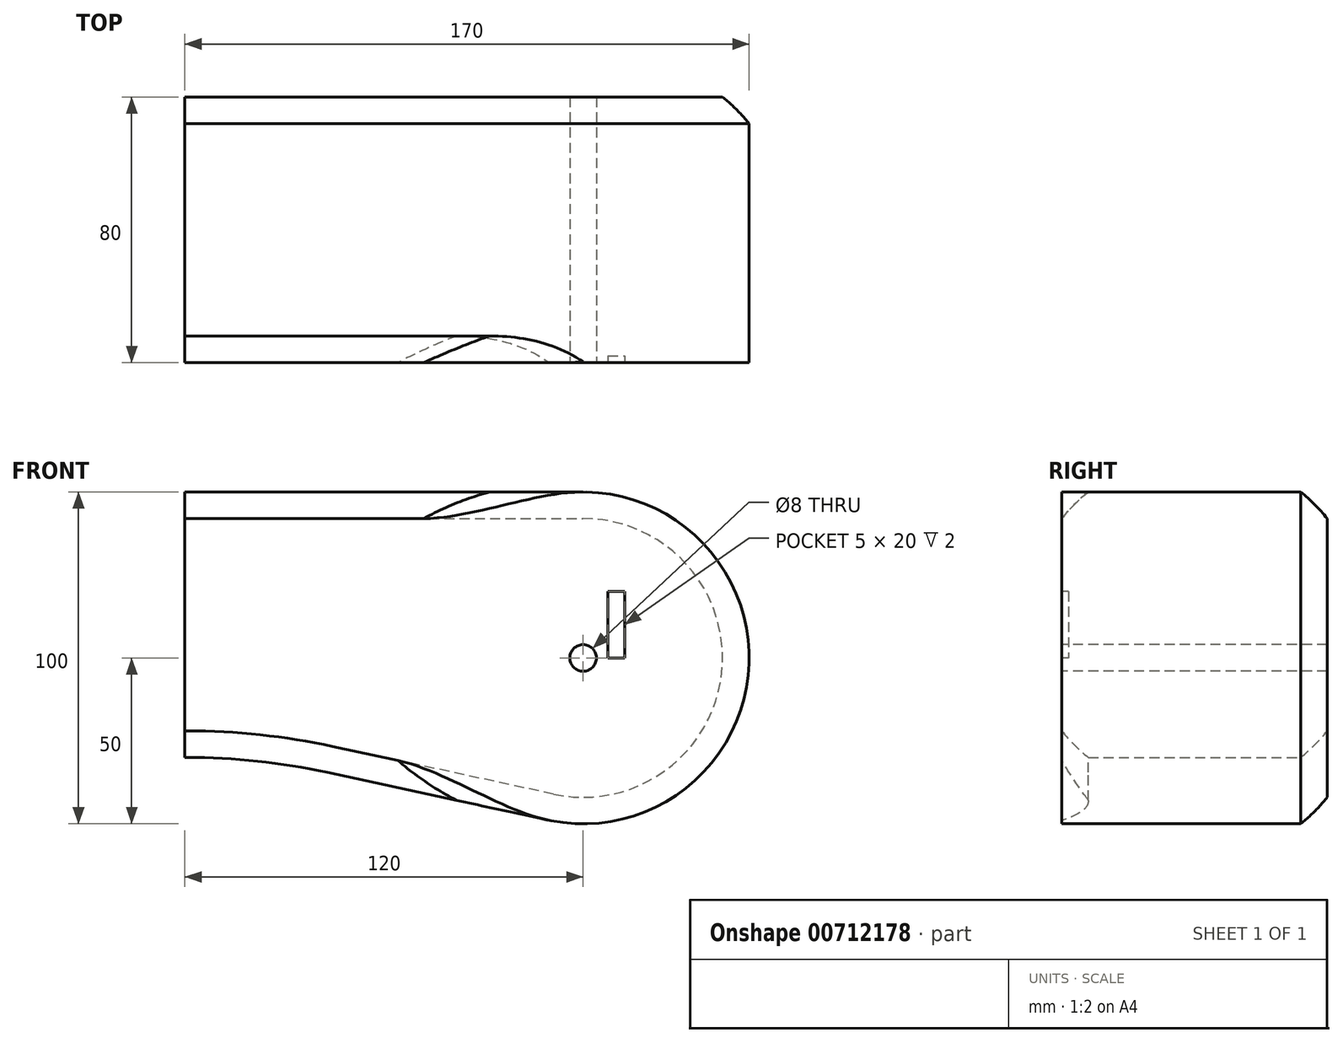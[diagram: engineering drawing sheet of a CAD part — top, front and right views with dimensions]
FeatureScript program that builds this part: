
annotation { "Feature Type Name" : "Feature", "Feature Type Description" : "" }
export const myFeature = defineFeature(function(context is Context, id is Id, definition is map)
    precondition{}
    {
        {
            var Q0;
            Q0=qCreatedBy(makeId("Front.planeOp"),FACE);
            var sketch = newSketch(context, id + "F0", { "sketchPlane" : qUnion([Q0])});
            skArc(sketch, "E0", {"start": v(-10.55, -48.87) * mm, "mid": v(49.72, -5.3) * mm, "end": v(0, 50) * mm});
            skLineSegment(sketch, "E1", {"start": v(0, 50) * mm, "end": v(-120, 50) * mm});
            skLineSegment(sketch, "E2", {"start": v(-120, 50) * mm, "end": v(-120, -30) * mm});
            skLineSegment(sketch, "E3", {"start": v(-120, -30) * mm, "end": v(-98, -30) * mm});
            skLineSegment(sketch, "E4", {"start": v(-98, -30) * mm, "end": v(-10.55, -48.87) * mm});
            skSolve(sketch);
        }
        {
            var Q0;
            Q0 = qSketchRegion(id + "F0", true);
            extrude(context, id + "F1", {"entities" : qUnion([Q0]), "depth" : 80 * mm, "offsetDistance" : 25 * mm, "symmetric" : true});
        }
        {
            var Q0;
            Q0=makeQuery(id+"F1.opExtrude","SWEPT_EDGE",EDGE,{"disambiguationData":[OSD([sQuery(id+"F0.wireOp",EDGE,"E3"),sQuery(id+"F0.wireOp",EDGE,"E4")])]});
            fillet(context, id + "F2", {"entities" : qUnion([Q0]), "radius" : 200 * mm, "tangentPropagation" : true, "allowEdgeOverflow" : false});
        }
        {
            var Q0;
            Q0=makeQuery(id+"F1.opExtrude","SWEPT_FACE",FACE,{"disambiguationData":[OSD([sQuery(id+"F0.wireOp",EDGE,"E2")])]});
            var sketch = newSketch(context, id + "F3", { "sketchPlane" : qUnion([Q0])});
            skLineSegment(sketch, "E5", {"start": v(0, 50) * mm, "end": v(0, -30) * mm, "construction": true});
            skArc(sketch, "E6", {"start": v(-32, 50) * mm, "mid": v(-36.22, 46.22) * mm, "end": v(-40, 42) * mm});
            skLineSegment(sketch, "E7", {"start": v(-40, 50) * mm, "end": v(-40, 42) * mm});
            skLineSegment(sketch, "E8", {"start": v(-40, 50) * mm, "end": v(-32, 50) * mm});
            skLineSegment(sketch, "E9.MirrorCS", {"start": v(40, 50) * mm, "end": v(40, 42) * mm});
            skArc(sketch, "E10.MirrorCS", {"start": v(32, 50) * mm, "mid": v(36.22, 46.22) * mm, "end": v(40, 42) * mm});
            skLineSegment(sketch, "E11.MirrorCS", {"start": v(40, 50) * mm, "end": v(32, 50) * mm});
            skSolve(sketch);
        }
        {
            var Q0;
            Q0 = qSketchRegion(id + "F3", true);
            var Q1;
            Q1=makeQuery(id+"F1.opExtrude","CAP_EDGE",EDGE,{"disambiguationData":[OSD([sQuery(id+"F0.wireOp",EDGE,"E1")])],"isStart":true});
            var Q2;
            Q2=makeQuery(id+"F1.opExtrude","CAP_EDGE",EDGE,{"disambiguationData":[OSD([sQuery(id+"F0.wireOp",EDGE,"E0")])],"isStart":true});
            var Q3;
            Q3=makeQuery(id+"F1.opExtrude","CAP_EDGE",EDGE,{"disambiguationData":[OSD([sQuery(id+"F0.wireOp",EDGE,"E4")])],"isStart":true});
            var Q4;
            Q4=makeQuery(id+"F1.opExtrude","CAP_EDGE",EDGE,{"disambiguationData":[OSD([sQuery(id+"F0.wireOp",EDGE,"E3")])],"isStart":true});
            var Q5;
            {var subQ0=sQuery(id+"F0.wireOp",EDGE,"E4");var subQ1=sQuery(id+"F0.wireOp",EDGE,"E3");Q5=makeQuery(id+"F2.opFillet","BLEND_EDGE",EDGE,{"blendedFrom":[makeQuery(id+"F1.opExtrude","SWEPT_EDGE",EDGE,{"disambiguationData":[OSD([subQ1,subQ0])]}),makeQuery(id+"F1.opExtrude","CAP_FACE",FACE,{"disambiguationData":[OSD([sQuery(id+"F0.wireOp",EDGE,"E0"),sQuery(id+"F0.wireOp",EDGE,"E1"),sQuery(id+"F0.wireOp",EDGE,"E2"),subQ1,subQ0])],"isStart":true})],"blendedInto":[makeQuery(id+"F1.opExtrude","CAP_FACE",FACE,{"disambiguationData":[OSD([sQuery(id+"F0.wireOp",EDGE,"E0"),sQuery(id+"F0.wireOp",EDGE,"E1"),sQuery(id+"F0.wireOp",EDGE,"E2"),subQ1,subQ0])],"isStart":true})]});}
            sweep(context, id + "F4", {"operationType" : NewBodyOperationType.REMOVE, "profiles" : qUnion([Q0]), "path" : qUnion([Q1, Q2, Q3, Q4, Q5])});
        }
        {
            var Q0;
            Q0=makeQuery(id+"F1.opExtrude","CAP_FACE",FACE,{"disambiguationData":[OSD([sQuery(id+"F0.wireOp",EDGE,"E0"),sQuery(id+"F0.wireOp",EDGE,"E1"),sQuery(id+"F0.wireOp",EDGE,"E2"),sQuery(id+"F0.wireOp",EDGE,"E3"),sQuery(id+"F0.wireOp",EDGE,"E4")])],"isStart":false});
            var sketch = newSketch(context, id + "F5", { "sketchPlane" : qUnion([Q0])});
            skCircle(sketch, "E12", {"center": v(0, 0) * mm, "radius": 50 * mm});
            skSolve(sketch);
        }
        {
            var Q0;
            Q0 = qSketchRegion(id + "F5", true);
            extrude(context, id + "F6", {"entities" : qUnion([Q0]), "operationType" : NewBodyOperationType.ADD, "oppositeDirection" : true, "depth" : 25 * mm, "offsetDistance" : 25 * mm});
        }
        {
            var Q0;
            Q0=makeQuery(id+"F6.boolean.opBoolean","INTERSECT",EDGE,{"derivedFrom":[makeQuery(id+"F4.boolean.opBoolean","COPY",FACE,{"derivedFrom":makeQuery(id+"F4.opSweep","SWEPT_FACE",FACE,{"disambiguationData":[OSD([sQuery(id+"F0.wireOp",EDGE,"E1"),sQuery(id+"F3.wireOp",EDGE,"E10.MirrorCS")])]})}),makeQuery(id+"F6.opExtrude","SWEPT_FACE",FACE,{"disambiguationData":[OSD([sQuery(id+"F5.wireOp",EDGE,"E12")])]})]});
            var Q1;
            Q1=makeQuery(id+"F6.boolean.opBoolean","INTERSECT",EDGE,{"derivedFrom":[makeQuery(id+"F4.boolean.opBoolean","COPY",FACE,{"derivedFrom":makeQuery(id+"F4.opSweep","SWEPT_FACE",FACE,{"disambiguationData":[OSD([sQuery(id+"F0.wireOp",EDGE,"E4"),sQuery(id+"F3.wireOp",EDGE,"E10.MirrorCS")])]})}),makeQuery(id+"F6.opExtrude","SWEPT_FACE",FACE,{"disambiguationData":[OSD([sQuery(id+"F5.wireOp",EDGE,"E12")])]})]});
            fillet(context, id + "F7", {"entities" : qUnion([Q0, Q1]), "radius" : 25 * mm, "tangentPropagation" : true, "allowEdgeOverflow" : false});
        }
        {
            var Q0;
            Q0=makeQuery(id+"F6.boolean.opBoolean","MERGE",FACE,{"derivedFrom":[makeQuery(id+"F1.opExtrude","CAP_FACE",FACE,{"disambiguationData":[OSD([sQuery(id+"F0.wireOp",EDGE,"E0"),sQuery(id+"F0.wireOp",EDGE,"E1"),sQuery(id+"F0.wireOp",EDGE,"E2"),sQuery(id+"F0.wireOp",EDGE,"E3"),sQuery(id+"F0.wireOp",EDGE,"E4")])],"isStart":false}),makeQuery(id+"F6.opExtrude","CAP_FACE",FACE,{"disambiguationData":[OSD([sQuery(id+"F5.wireOp",EDGE,"E12")])],"isStart":true})]});
            var sketch = newSketch(context, id + "F8", { "sketchPlane" : qUnion([Q0])});
            skCircle(sketch, "E13", {"center": v(0, 0) * mm, "radius": 4 * mm});
            skSolve(sketch);
        }
        {
            var Q0;
            Q0 = qSketchRegion(id + "F8", true);
            extrude(context, id + "F9", {"entities" : qUnion([Q0]), "operationType" : NewBodyOperationType.REMOVE, "endBound" : BoundingType.THROUGH_ALL, "oppositeDirection" : true, "depth" : 25 * mm, "offsetDistance" : 25 * mm});
        }
        {
            var Q0;
            Q0=makeQuery(id+"F6.boolean.opBoolean","MERGE",FACE,{"derivedFrom":[makeQuery(id+"F1.opExtrude","CAP_FACE",FACE,{"disambiguationData":[OSD([sQuery(id+"F0.wireOp",EDGE,"E0"),sQuery(id+"F0.wireOp",EDGE,"E1"),sQuery(id+"F0.wireOp",EDGE,"E2"),sQuery(id+"F0.wireOp",EDGE,"E3"),sQuery(id+"F0.wireOp",EDGE,"E4")])],"isStart":false}),makeQuery(id+"F6.opExtrude","CAP_FACE",FACE,{"disambiguationData":[OSD([sQuery(id+"F5.wireOp",EDGE,"E12")])],"isStart":true})]});
            var sketch = newSketch(context, id + "F10", { "sketchPlane" : qUnion([Q0])});
            skLineSegment(sketch, "E14.bottom", {"start": v(7.5, 20) * mm, "end": v(12.5, 20) * mm});
            skLineSegment(sketch, "E14.top", {"start": v(7.5, 0) * mm, "end": v(12.5, 0) * mm});
            skLineSegment(sketch, "E14.left", {"start": v(7.5, 20) * mm, "end": v(7.5, 0) * mm});
            skLineSegment(sketch, "E14.right", {"start": v(12.5, 20) * mm, "end": v(12.5, 0) * mm});
            skPoint(sketch, "E14.middle", {"position": v(10, 10) * mm});
            skSolve(sketch);
        }
        {
            var Q0;
            Q0 = qSketchRegion(id + "F10", true);
            extrude(context, id + "F11", {"entities" : qUnion([Q0]), "operationType" : NewBodyOperationType.REMOVE, "oppositeDirection" : true, "depth" : 2 * mm, "offsetDistance" : 25 * mm});
        }
    });
